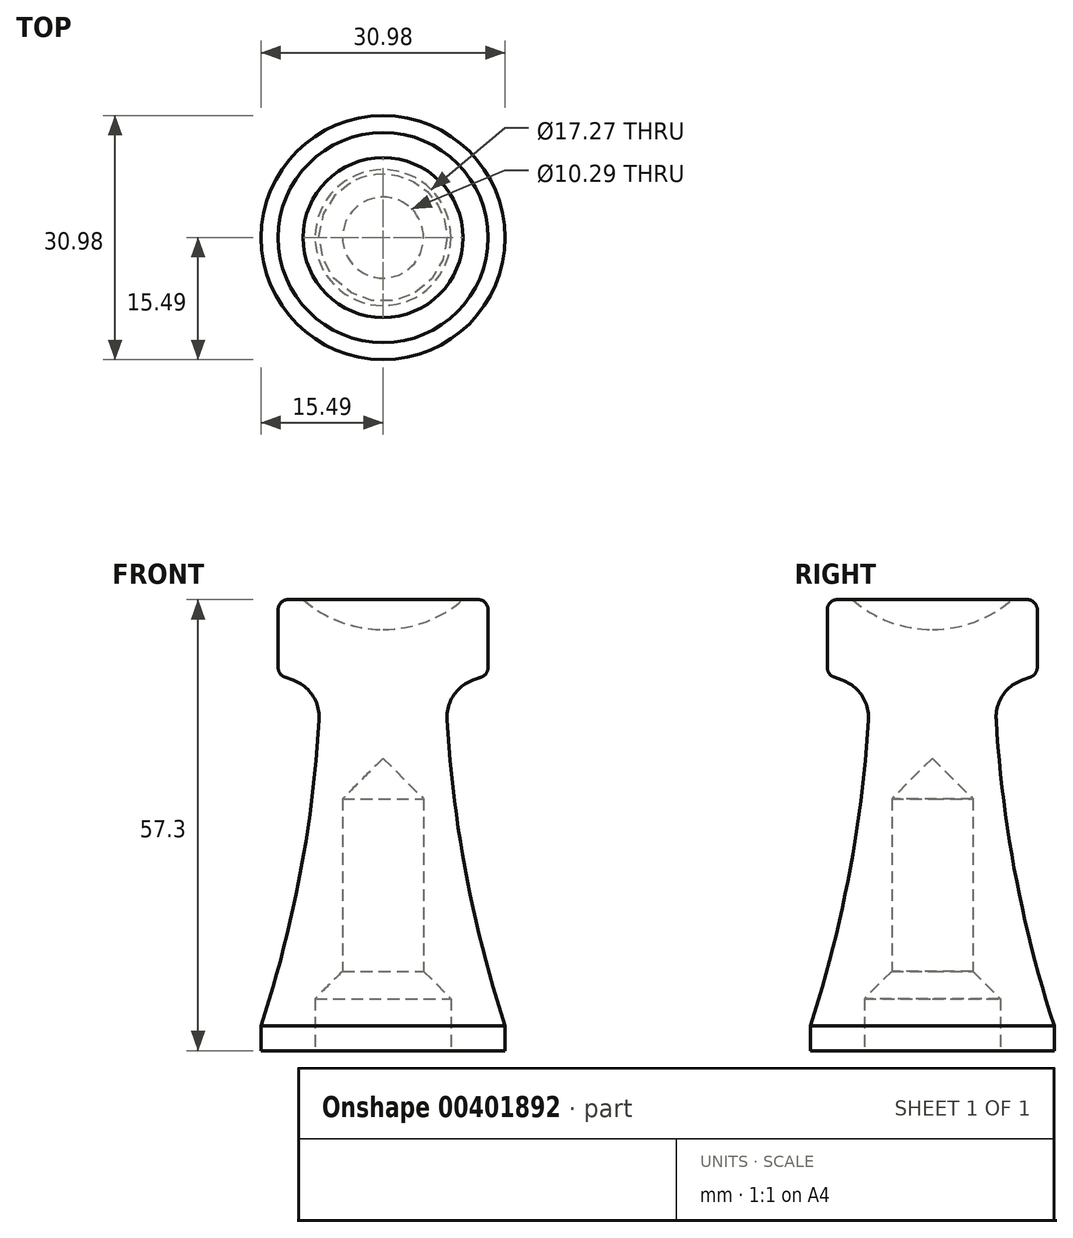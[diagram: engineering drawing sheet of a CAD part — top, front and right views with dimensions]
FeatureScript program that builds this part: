
annotation { "Feature Type Name" : "Feature", "Feature Type Description" : "" }
export const myFeature = defineFeature(function(context is Context, id is Id, definition is map)
    precondition{}
    {
        {
            var Q0;
            Q0=qCreatedBy(makeId("Front.planeOp"),FACE);
            var sketch = newSketch(context, id + "F0", { "sketchPlane" : qUnion([Q0])});
            skLineSegment(sketch, "E0", {"start": v(-8.64, 0) * mm, "end": v(-15.5, 0) * mm});
            skLineSegment(sketch, "E1", {"start": v(-15.5, 0) * mm, "end": v(-15.5, 3.17) * mm});
            skArc(sketch, "E2", {"start": v(-15.5, 3.17) * mm, "mid": v(-10.22, 24.23) * mm, "end": v(-7.94, 45.81) * mm});
            skLineSegment(sketch, "E3", {"start": v(0, 37.15) * mm, "end": v(0, 60.5) * mm, "construction": true});
            skLineSegment(sketch, "E4", {"start": v(-7.94, 45.81) * mm, "end": v(-6.48, 87.5) * mm, "construction": true});
            skLineSegment(sketch, "E5", {"start": v(-7.94, 45.81) * mm, "end": v(-13.34, 47.78) * mm});
            skLineSegment(sketch, "E6", {"start": v(-13.34, 47.78) * mm, "end": v(-13.34, 57.3) * mm});
            skLineSegment(sketch, "E7", {"start": v(-13.34, 57.3) * mm, "end": v(-10.16, 57.3) * mm});
            skLineSegment(sketch, "E8", {"start": v(0, 53.5) * mm, "end": v(0, 37.15) * mm});
            skArc(sketch, "E9", {"start": v(-10.16, 57.3) * mm, "mid": v(-5.43, 54.48) * mm, "end": v(0, 53.5) * mm});
            skLineSegment(sketch, "E10", {"start": v(-5.14, 10.1) * mm, "end": v(-5.14, 32) * mm});
            skLineSegment(sketch, "E11", {"start": v(-5.14, 32) * mm, "end": v(0, 37.15) * mm});
            skLineSegment(sketch, "E12", {"start": v(0, 37.15) * mm, "end": v(0, 0) * mm, "construction": true});
            skLineSegment(sketch, "E13", {"start": v(0, 0) * mm, "end": v(-8.64, 0) * mm, "construction": true});
            skLineSegment(sketch, "E14", {"start": v(-5.14, 10.1) * mm, "end": v(-8.64, 6.6) * mm});
            skLineSegment(sketch, "E15", {"start": v(-8.64, 6.6) * mm, "end": v(-8.64, 0) * mm});
            skSolve(sketch);
        }
        {
            var Q0;
            Q0 = qSketchRegion(id + "F0", true);
            var Q1;
            Q1=sQuery(id+"F0.wireOp",EDGE,"E3");
            revolve(context, id + "F1", {"entities" : qUnion([Q0]), "axis" : qUnion([Q1]), "revolveType" : RevolveType.FULL});
        }
        {
            var Q0;
            Q0=makeQuery(id+"F1.opRevolve","SWEPT_EDGE",EDGE,{"disambiguationData":[OSD([sQuery(id+"F0.wireOp",EDGE,"E2"),sQuery(id+"F0.wireOp",EDGE,"E5")])]});
            fillet(context, id + "F2", {"entities" : qUnion([Q0]), "radius" : 5.08 * mm, "tangentPropagation" : true, "allowEdgeOverflow" : false});
        }
        {
            var Q0;
            Q0=makeQuery(id+"F1.opRevolve","SWEPT_EDGE",EDGE,{"disambiguationData":[OSD([sQuery(id+"F0.wireOp",EDGE,"E5"),sQuery(id+"F0.wireOp",EDGE,"E6")])]});
            var Q1;
            Q1=makeQuery(id+"F1.opRevolve","SWEPT_EDGE",EDGE,{"disambiguationData":[OSD([sQuery(id+"F0.wireOp",EDGE,"E6"),sQuery(id+"F0.wireOp",EDGE,"E7")])]});
            fillet(context, id + "F3", {"entities" : qUnion([Q0, Q1]), "radius" : 1.27 * mm, "tangentPropagation" : true, "allowEdgeOverflow" : false});
        }
    });
